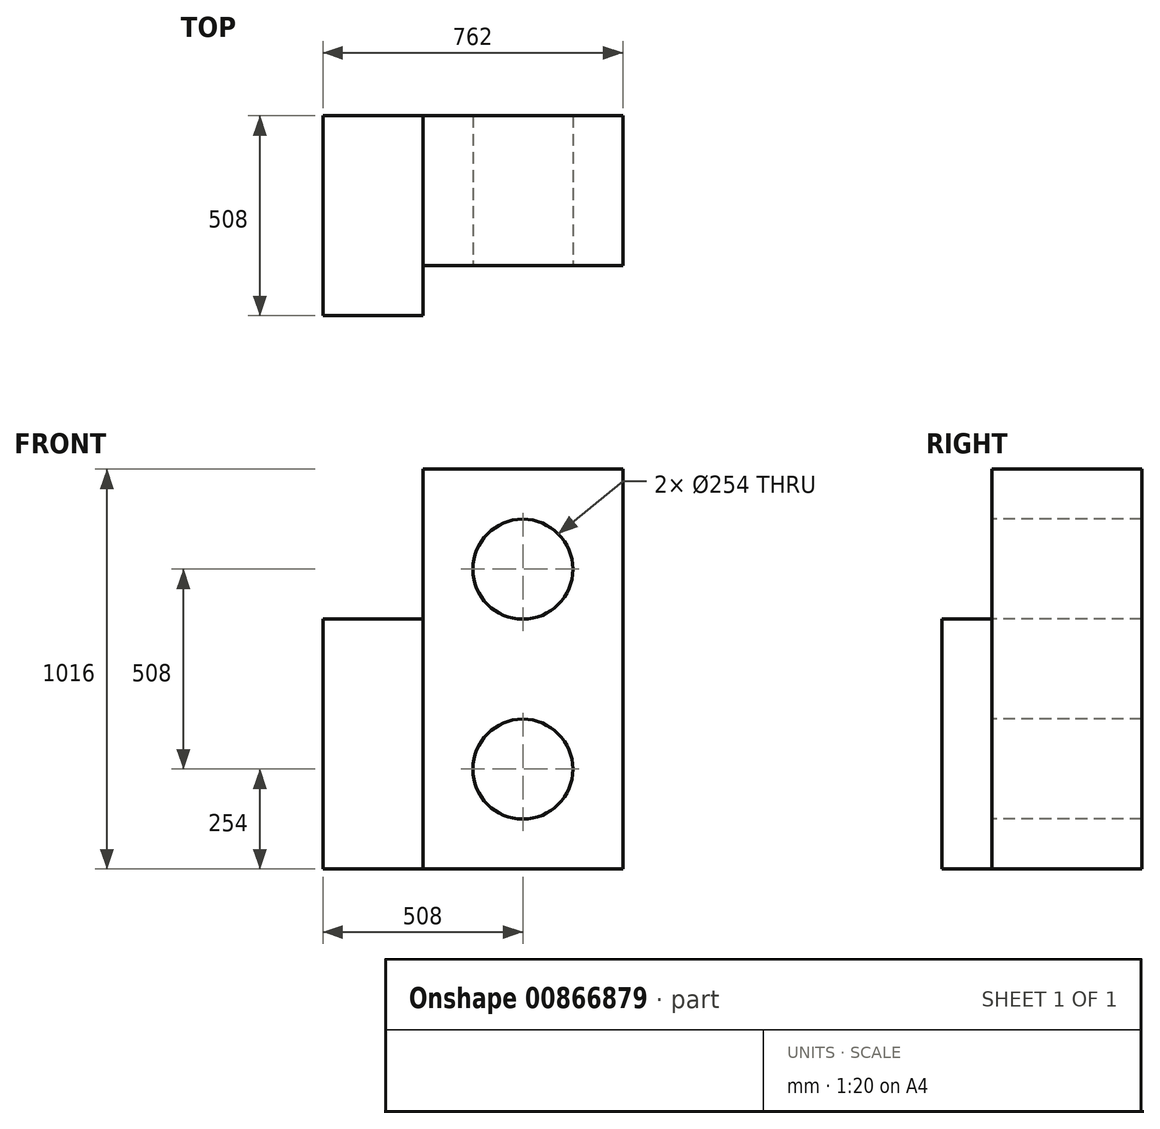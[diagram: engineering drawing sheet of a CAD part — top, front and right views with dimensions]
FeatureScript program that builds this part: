
annotation { "Feature Type Name" : "Feature", "Feature Type Description" : "" }
export const myFeature = defineFeature(function(context is Context, id is Id, definition is map)
    precondition{}
    {
        {
            var Q0;
            Q0=qCreatedBy(makeId("Front.planeOp"),FACE);
            var sketch = newSketch(context, id + "F0", { "sketchPlane" : qUnion([Q0])});
            skLineSegment(sketch, "E0.bottom", {"start": v(0, 0) * mm, "end": v(508, 0) * mm});
            skLineSegment(sketch, "E0.top", {"start": v(0, 1016) * mm, "end": v(508, 1016) * mm});
            skLineSegment(sketch, "E0.left", {"start": v(0, 0) * mm, "end": v(0, 1016) * mm});
            skLineSegment(sketch, "E0.right", {"start": v(508, 0) * mm, "end": v(508, 1016) * mm});
            skCircle(sketch, "E1", {"center": v(254, 254) * mm, "radius": 127 * mm});
            skPoint(sketch, "E1.centerSnap0", {"position": v(254, 0) * mm});
            skCircle(sketch, "E2", {"center": v(254, 762) * mm, "radius": 127 * mm});
            skPoint(sketch, "E2.centerSnap0", {"position": v(254, 1016) * mm});
            skSolve(sketch);
        }
        {
            var Q0;
            Q0=makeQuery(id+"F0.imprint","IMPRINT",FACE,{"disambiguationData":[TD([[makeQuery(id+"F0.imprint","IMPRINT",EDGE,{"derivedFrom":sQuery(id+"F0.wireOp",EDGE,"E0.bottom")}),1.0]])]});
            extrude(context, id + "F1", {"entities" : qUnion([Q0]), "oppositeDirection" : true, "depth" : 381 * mm, "offsetDistance" : 25.4 * mm});
        }
        {
            var Q0;
            Q0=makeQuery(id+"F1.opExtrude","SWEPT_FACE",FACE,{"disambiguationData":[OSD([sQuery(id+"F0.wireOp",EDGE,"E0.left")])]});
            var sketch = newSketch(context, id + "F2", { "sketchPlane" : qUnion([Q0])});
            skLineSegment(sketch, "E3.bottom", {"start": v(-381, 0) * mm, "end": v(127, 0) * mm});
            skLineSegment(sketch, "E3.top", {"start": v(-381, 635) * mm, "end": v(127, 635) * mm});
            skLineSegment(sketch, "E3.left", {"start": v(-381, 0) * mm, "end": v(-381, 635) * mm});
            skLineSegment(sketch, "E3.right", {"start": v(127, 0) * mm, "end": v(127, 635) * mm});
            skSolve(sketch);
        }
        {
            var Q0;
            {var subQ3=sQuery(id+"F2.wireOp",EDGE,"E3.right");Q0=makeQuery(id+"F2.imprint","IMPRINT",FACE,{"disambiguationData":[TD([[makeQuery(id+"F2.imprint","IMPRINT",EDGE,{"derivedFrom":subQ3}),1.0]])]});}
            var Q1;
            {var subQ4=sQuery(id+"F2.wireOp",EDGE,"E3.left");Q1=makeQuery(id+"F2.imprint","IMPRINT",FACE,{"disambiguationData":[TD([[makeQuery(id+"F2.imprint","IMPRINT",EDGE,{"derivedFrom":subQ4}),-1.0]])]});}
            extrude(context, id + "F3", {"entities" : qUnion([Q0, Q1]), "operationType" : NewBodyOperationType.ADD, "depth" : 254 * mm, "offsetDistance" : 25.4 * mm});
        }
    });
